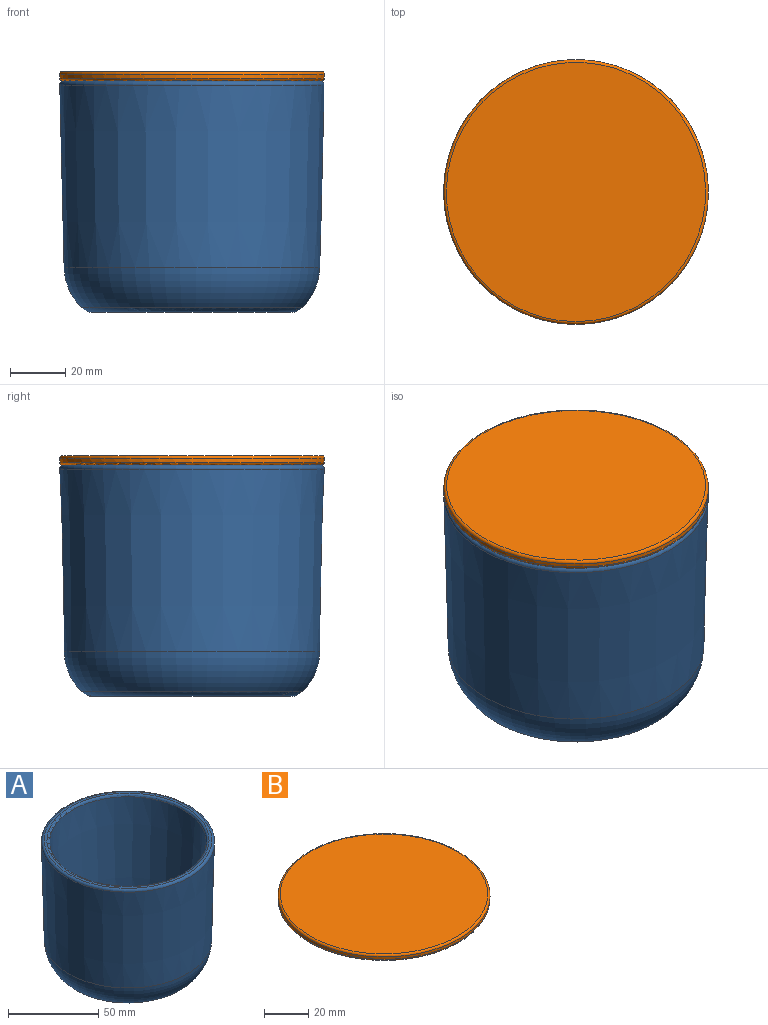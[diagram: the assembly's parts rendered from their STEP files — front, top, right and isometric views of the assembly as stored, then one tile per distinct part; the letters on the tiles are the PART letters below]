
ASSEMBLY  parts=2 mates=1
PART A: 11 faces, bbox 103.8x103.8x88.2 mm
  f0: cone r=43.5mm half-angle=3.5deg, axis (0,0,1), area 18136.1mm2, adj f3,f6
  f1: torus R=35.76mm, axis (0,0,1), area 1107.2mm2, adj f8,f10
  f2: plane 72.35x72.35mm, normal (0,0,1), area 4111.6mm2, adj f3
  f3: torus R=36.18mm, axis (0,0,-1), area 1082.9mm2, adj f0,f2
  f4: torus R=46.46mm, axis (0,0,-1), area 712.8mm2, adj f5,f7
  f5: plane 92.93x92.93mm, normal (0,0,1), area 445.6mm2, adj f4,f6
  f6: torus R=44.91mm, axis (0,0,-1), area 625.9mm2, adj f0,f5
  f7: cone r=46mm half-angle=1.4deg, axis (0,0,1), area 19603.5mm2, adj f4,f9
  f8: cone r=38.2mm half-angle=45.7deg, axis (0,0,1), area 42.3mm2, adj f1,f9
  f9: torus R=25.4mm, axis (0,0,-1), area 4507.6mm2, adj f7,f8
  f10: sphere r=426.91mm, area 4023.6mm2, adj f1
PART B: 10 faces, bbox 103.9x103.9x6.4 mm
  f0: plane 94x94mm, normal (0,0,1), area 6939.8mm2, adj f8
  f1: plane 78x78mm, normal (0,0,-1), area 4778.4mm2, adj f2
  f2: cylinder r=39mm len=78mm, axis (0,0,-1), area 490.1mm2, adj f1,f3
  f3: plane 82x82mm, normal (0,0,-1), area 502.7mm2, adj f2,f9
  f4: cylinder r=42mm len=84mm, axis (0,0,-1), area 527.8mm2, adj f5,f9
  f5: plane 94x94mm, normal (0,0,-1), area 1398mm2, adj f4,f7
  f6: cylinder r=48mm len=96mm, axis (0,0,-1), area 422.2mm2, adj f7,f8
  f7: torus R=47mm, axis (0,0,1), area 470.2mm2, adj f5,f6
  f8: torus R=47mm, axis (0,0,-1), area 470.2mm2, adj f0,f6
  f9: torus R=41mm, axis (0,0,1), area 410.9mm2, adj f3,f4
PLACE A t=(-5.25,1.01,-34.08)mm fixed
PLACE B rot(axis=(0,0,1),90deg) t=(-5.25,1.01,46.92)mm
MATE planar A.f0 <-> B.f2  axis (0,0,1) through (-5.25,1.01,49.92)mm
